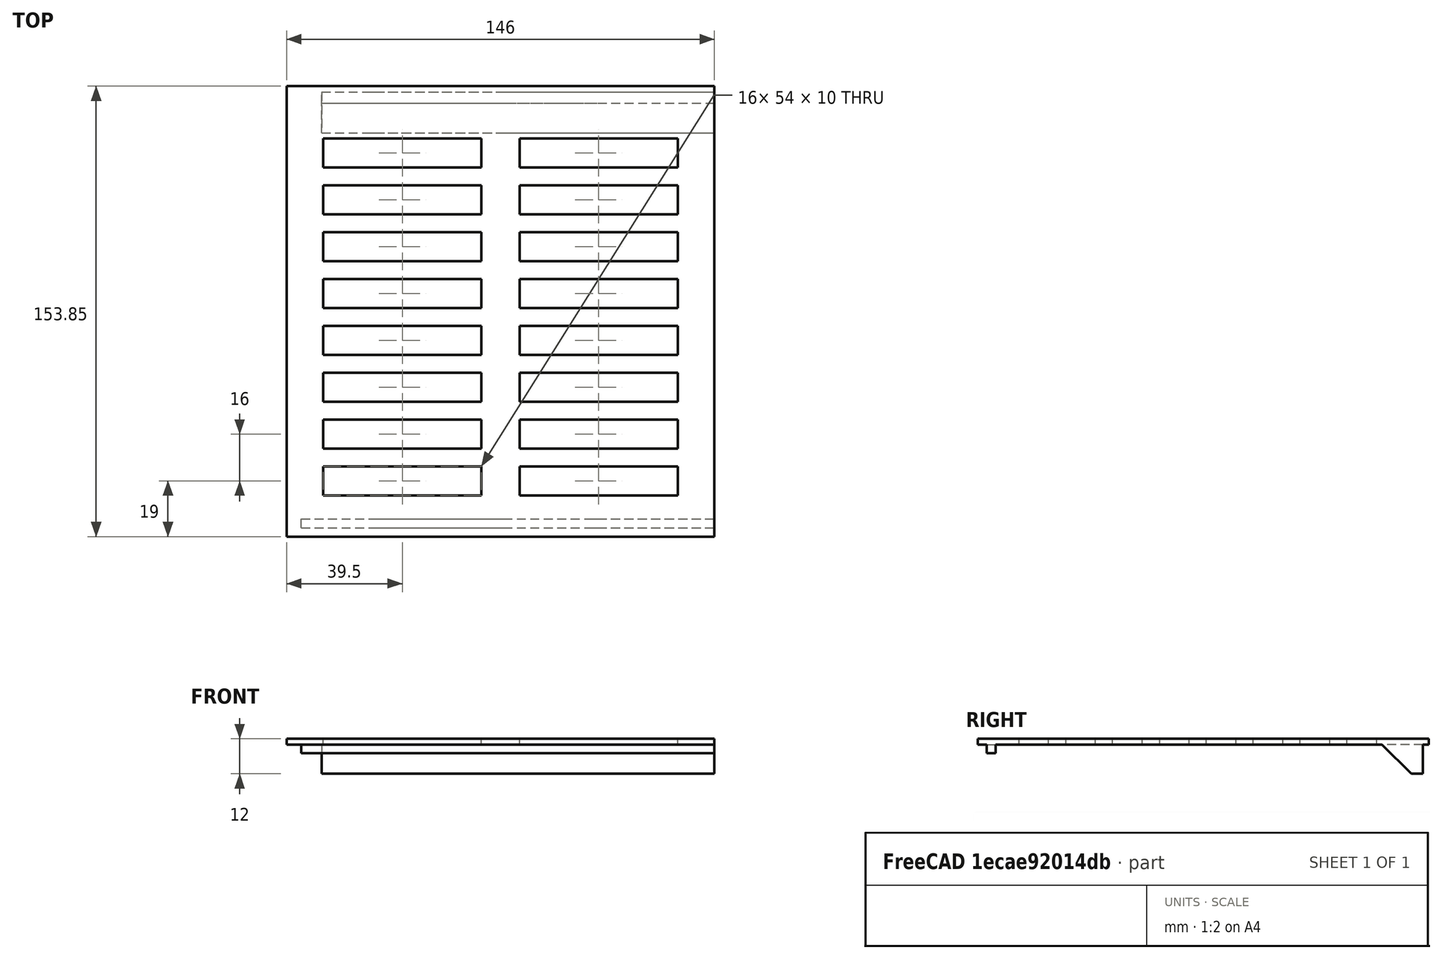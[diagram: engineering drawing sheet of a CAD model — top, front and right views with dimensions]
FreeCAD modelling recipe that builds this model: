
FCSTD DOCUMENT  (FreeCAD 0.17R13522 (Git))
Label: lateral_derecho_v2
License: CreativeCommons Attribution-ShareAlike
LicenseURL: http://creativecommons.org/licenses/by-sa/4.0/
objects: Part::Feature×4, Part::Box×3, Part::Cut×3, Part::MultiFuse×2, Part::FeaturePython×1
note: 13 computed .brp shape members not serialized (recipe doc carries the construction recipe); baked Part::Feature solids carry a one-line shape summary decoded from their .brp

FEATURE [Part::Feature] Cut003001  label="Cut004"
  shape: bbox 30 x 153.9 x 12 mm, 47 faces (baked)
FEATURE [Part::Feature] Cut004001  label="Cut005"
  shape: bbox 108 x 153.9 x 12 mm, 79 faces (baked)
FEATURE [Part::Feature] Cut004002  label="Cut006"
  shape: bbox 72 x 153.9 x 12 mm, 47 faces (baked)
FEATURE [Part::Box] Box  label="Cube"
  AttacherType = Attacher::AttachEngine3D
  Height = 30
  Length = 30
  Placement = pos=(30,-16,-18) rot=(0,0,1;0rad)
  Width = 200
FEATURE [Part::Cut] Cut
  Base = -> Cut004001
  Placement = pos=(-30,0,0) rot=(0,0,1;0rad)
  Tool = -> Box
FEATURE [Part::Box] Box001  label="Cube001"
  AttacherType = Attacher::AttachEngine3D
  Height = 20
  Length = 1
  Placement = pos=(67.5,14,-10) rot=(0,0,1;0rad)
  Width = 10
FEATURE [Part::FeaturePython] Array  # Draft array (typed FeaturePython)
  Angle = 360
  ArrayType = 0
  Axis = (0,0,1)
  Base = -> Box001
  Center = (0,0,0)
  Fuse = false
  IntervalAxis = (0,0,0)
  IntervalX = (14,0,0)
  IntervalY = (0,16,0)
  IntervalZ = (0,0,0)
  NumberPolar = 1
  NumberX = 2
  NumberY = 8
  NumberZ = 1
FEATURE [Part::Cut] Cut004003
  Base = -> Cut
  Placement = pos=(-2,0,0) rot=(0,0,1;0rad)
  Tool = -> Array
FEATURE [Part::Box] Box002  label="Cube002"
  AttacherType = Attacher::AttachEngine3D
  Height = 31
  Length = 30
  Placement = pos=(138,-15,0) rot=(0,0,1;0rad)
  Width = 200
FEATURE [Part::Cut] Cut004004
  Base = -> Cut004002
  Placement = pos=(-64,0,0) rot=(0,0,1;0rad)
  Tool = -> Box002
FEATURE [Part::MultiFuse] Fusion
  Shapes = -> [Cut003001,Cut004003]
FEATURE [Part::MultiFuse] Fusion001
  Shapes = -> [Fusion,Cut004004]
FEATURE [Part::Feature] Fusion001001  label="Fusion002"
  shape: bbox 146 x 153.9 x 12 mm, 79 faces (baked)
